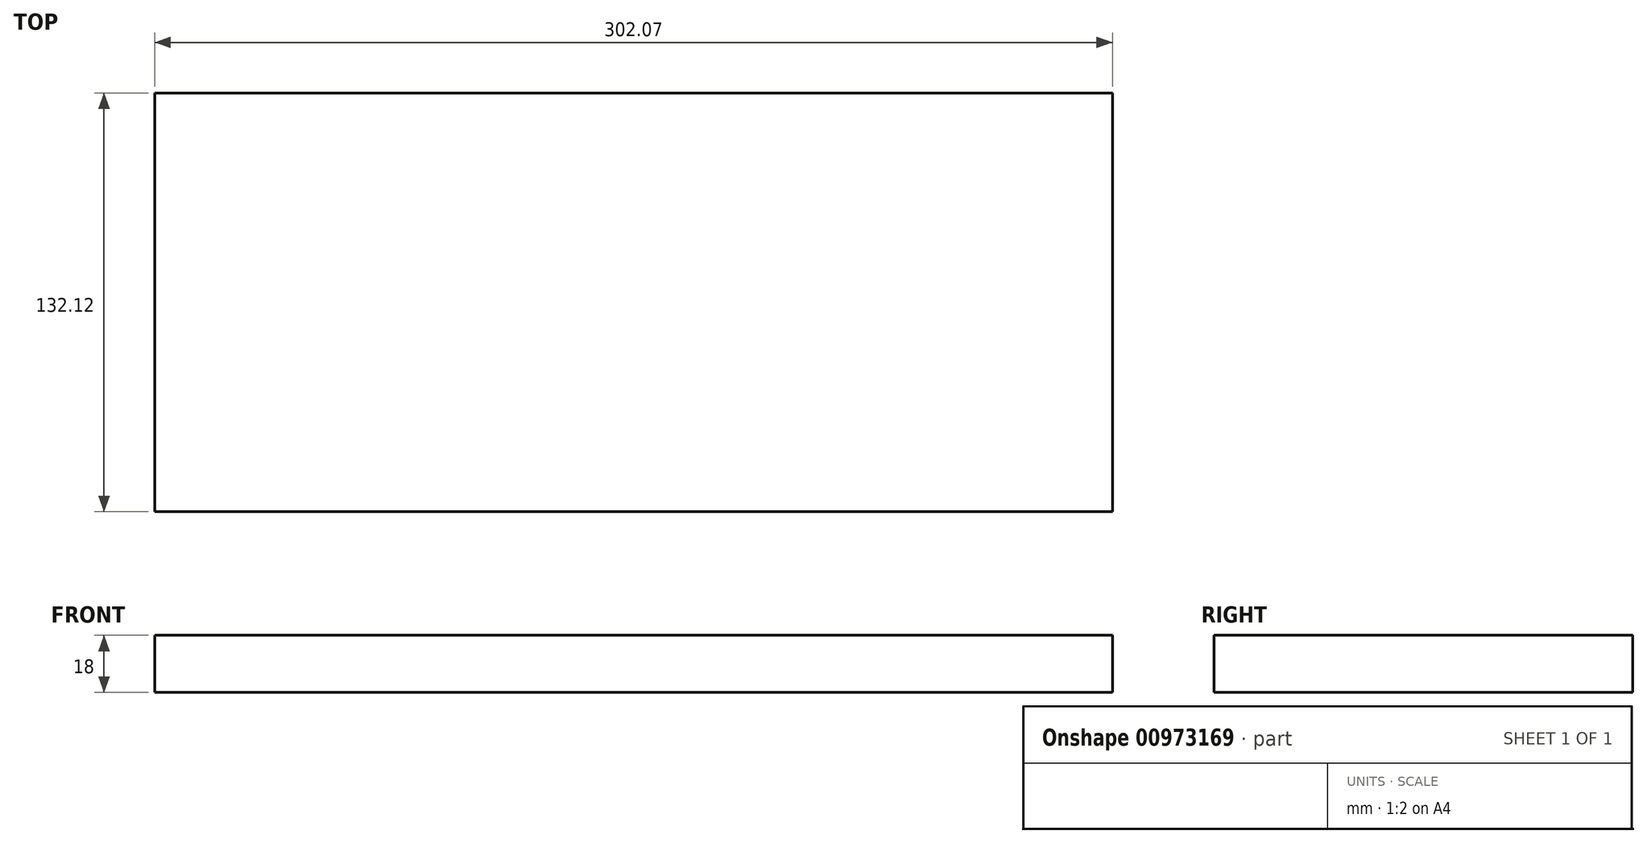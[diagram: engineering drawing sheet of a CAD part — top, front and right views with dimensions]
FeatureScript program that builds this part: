
annotation { "Feature Type Name" : "Feature", "Feature Type Description" : "" }
export const myFeature = defineFeature(function(context is Context, id is Id, definition is map)
    precondition{}
    {
        {
            var Q0;
            Q0=qCreatedBy(makeId("Top.planeOp"),FACE);
            var sketch = newSketch(context, id + "F0", { "sketchPlane" : qUnion([Q0])});
            skLineSegment(sketch, "E0.bottom", {"start": v(-121.96, 25.2) * mm, "end": v(180.1, 25.2) * mm});
            skLineSegment(sketch, "E0.top", {"start": v(-121.96, -106.92) * mm, "end": v(180.1, -106.92) * mm});
            skLineSegment(sketch, "E0.left", {"start": v(-121.96, 25.2) * mm, "end": v(-121.96, -106.92) * mm});
            skLineSegment(sketch, "E0.right", {"start": v(180.1, 25.2) * mm, "end": v(180.1, -106.92) * mm});
            skSolve(sketch);
        }
        {
            var Q0;
            Q0 = qSketchRegion(id + "F0", true);
            extrude(context, id + "F1", {"entities" : qUnion([Q0]), "depth" : 18 * mm, "offsetDistance" : 25.4 * mm});
        }
    });
